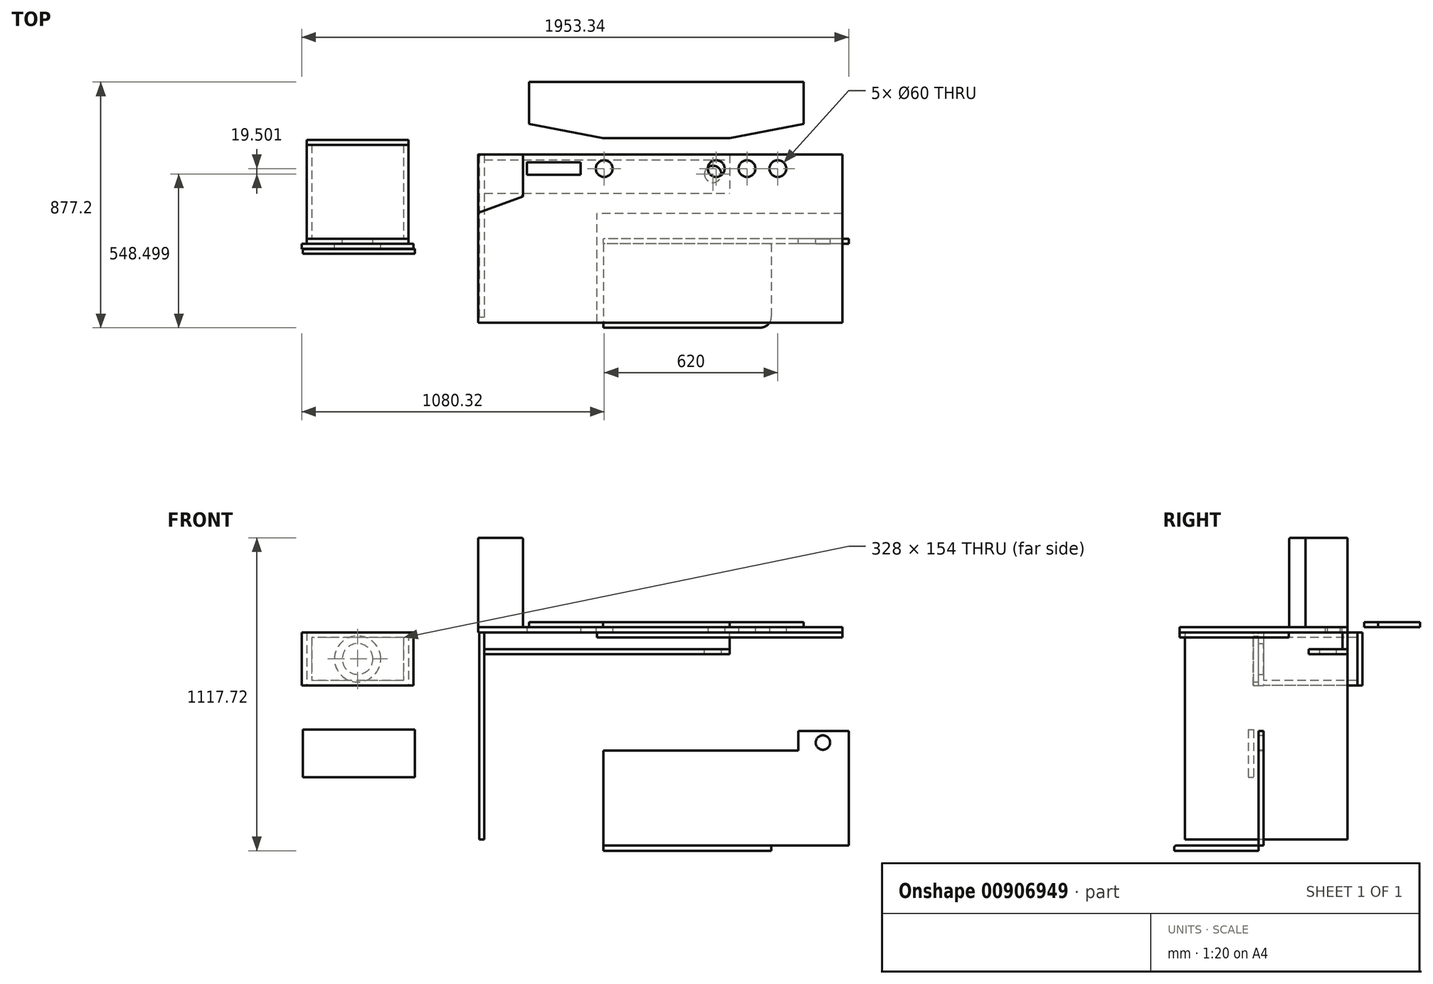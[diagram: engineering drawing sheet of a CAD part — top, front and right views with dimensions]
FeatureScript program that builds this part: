
annotation { "Feature Type Name" : "Feature", "Feature Type Description" : "" }
export const myFeature = defineFeature(function(context is Context, id is Id, definition is map)
    precondition{}
    {
        {
            var Q0;
            Q0=qCreatedBy(makeId("Top.planeOp"),FACE);
            var sketch = newSketch(context, id + "F0", { "sketchPlane" : qUnion([Q0])});
            skLineSegment(sketch, "E0.bottom", {"start": v(650, -300) * mm, "end": v(-650, -300) * mm});
            skLineSegment(sketch, "E0.top", {"start": v(650, 300) * mm, "end": v(-650, 300) * mm});
            skLineSegment(sketch, "E0.left", {"start": v(650, -300) * mm, "end": v(650, 300) * mm});
            skLineSegment(sketch, "E0.right", {"start": v(-650, -300) * mm, "end": v(-650, 300) * mm});
            skPoint(sketch, "E0.middle", {"position": v(0, 0) * mm});
            skLineSegment(sketch, "E1", {"start": v(-650, 250) * mm, "end": v(650, 250) * mm, "construction": true});
            skCircle(sketch, "E2", {"center": v(420, 250) * mm, "radius": 30 * mm});
            skCircle(sketch, "E3.1.0.0", {"center": v(-200, 250) * mm, "radius": 30 * mm});
            skCircle(sketch, "E3.2.0.0", {"center": v(200, 250) * mm, "radius": 30 * mm});
            skCircle(sketch, "E3.3.0.0", {"center": v(310, 250) * mm, "radius": 30 * mm});
            skLineSegment(sketch, "E3.direction1", {"start": v(-200, 250) * mm, "end": v(420, 250) * mm, "construction": true});
            skLineSegment(sketch, "E4.bottom", {"start": v(-284, 227.5) * mm, "end": v(-476, 227.5) * mm});
            skLineSegment(sketch, "E4.top", {"start": v(-284, 272.5) * mm, "end": v(-476, 272.5) * mm});
            skLineSegment(sketch, "E4.left", {"start": v(-284, 227.5) * mm, "end": v(-284, 272.5) * mm});
            skLineSegment(sketch, "E4.right", {"start": v(-476, 227.5) * mm, "end": v(-476, 272.5) * mm});
            skPoint(sketch, "E4.middle", {"position": v(-380, 250) * mm});
            skSolve(sketch);
        }
        {
            var Q0;
            Q0=qSketchRegion(id+"F0",true);
            extrude(context, id + "F1", {"entities" : qUnion([Q0]), "depth" : 18 * mm, "offsetDistance" : 25 * mm});
        }
        {
            var Q0;
            Q0=makeQuery(id+"F1.opExtrude","CAP_FACE",FACE,{"disambiguationData":[OSD([sQuery(id+"F0.wireOp",EDGE,"E0.bottom"),sQuery(id+"F0.wireOp",EDGE,"E0.top"),sQuery(id+"F0.wireOp",EDGE,"E0.left"),sQuery(id+"F0.wireOp",EDGE,"E0.right")])],"isStart":true});
            var sketch = newSketch(context, id + "F2", { "sketchPlane" : qUnion([Q0])});
            skLineSegment(sketch, "E5.bottom", {"start": v(-627.74, -300) * mm, "end": v(248.26, -300) * mm});
            skLineSegment(sketch, "E5.top", {"start": v(-627.74, -282) * mm, "end": v(248.26, -282) * mm});
            skLineSegment(sketch, "E5.left", {"start": v(-627.74, -300) * mm, "end": v(-627.74, -282) * mm});
            skLineSegment(sketch, "E5.right", {"start": v(248.26, -300) * mm, "end": v(248.26, -282) * mm});
            skSolve(sketch);
        }
        {
            var Q0;
            Q0=qSketchRegion(id+"F2",true);
            extrude(context, id + "F3", {"entities" : qUnion([Q0]), "depth" : 60 * mm, "offsetDistance" : 25 * mm});
        }
        {
            var Q0;
            Q0=makeQuery(id+"F3.opExtrude","CAP_FACE",FACE,{"disambiguationData":[OSD([sQuery(id+"F2.wireOp",EDGE,"E5.bottom"),sQuery(id+"F2.wireOp",EDGE,"E5.top"),sQuery(id+"F2.wireOp",EDGE,"E5.left"),sQuery(id+"F2.wireOp",EDGE,"E5.right")])],"isStart":false});
            var sketch = newSketch(context, id + "F4", { "sketchPlane" : qUnion([Q0])});
            skLineSegment(sketch, "E6.bottom", {"start": v(-627.74, -300) * mm, "end": v(248.26, -300) * mm});
            skLineSegment(sketch, "E6.top", {"start": v(-627.74, -162) * mm, "end": v(248.26, -162) * mm});
            skLineSegment(sketch, "E6.left", {"start": v(-627.74, -300) * mm, "end": v(-627.74, -162) * mm});
            skLineSegment(sketch, "E6.right", {"start": v(248.26, -300) * mm, "end": v(248.26, -162) * mm});
            skCircle(sketch, "E7", {"center": v(188.26, -230.5) * mm, "radius": 30 * mm});
            skSolve(sketch);
        }
        {
            var Q0;
            Q0=qSketchRegion(id+"F4",true);
            extrude(context, id + "F5", {"entities" : qUnion([Q0]), "depth" : 18 * mm, "offsetDistance" : 25 * mm});
        }
        {
            var Q0;
            Q0=makeQuery(id+"F3.opExtrude","SWEPT_FACE",FACE,{"disambiguationData":[OSD([sQuery(id+"F2.wireOp",EDGE,"E5.left")])]});
            var sketch = newSketch(context, id + "F6", { "sketchPlane" : qUnion([Q0])});
            skLineSegment(sketch, "E8.bottom", {"start": v(-300, 0) * mm, "end": v(280, 0) * mm});
            skLineSegment(sketch, "E8.top", {"start": v(-300, -740) * mm, "end": v(280, -740) * mm});
            skLineSegment(sketch, "E8.left", {"start": v(-300, 0) * mm, "end": v(-300, -740) * mm});
            skLineSegment(sketch, "E8.right", {"start": v(280, 0) * mm, "end": v(280, -740) * mm});
            skSolve(sketch);
        }
        {
            var Q0;
            Q0=qSketchRegion(id+"F6",true);
            extrude(context, id + "F7", {"entities" : qUnion([Q0]), "depth" : 18 * mm, "offsetDistance" : 25 * mm});
        }
        {
            var Q0;
            Q0=makeQuery(id+"F1.opExtrude","CAP_FACE",FACE,{"disambiguationData":[OSD([sQuery(id+"F0.wireOp",EDGE,"E0.bottom"),sQuery(id+"F0.wireOp",EDGE,"E0.top"),sQuery(id+"F0.wireOp",EDGE,"E0.left"),sQuery(id+"F0.wireOp",EDGE,"E0.right")])],"isStart":false});
            var sketch = newSketch(context, id + "F8", { "sketchPlane" : qUnion([Q0])});
            skLineSegment(sketch, "E9", {"start": v(-650, 300) * mm, "end": v(-650, 91.76) * mm});
            skLineSegment(sketch, "E10", {"start": v(-650, 91.76) * mm, "end": v(-490, 150) * mm});
            skLineSegment(sketch, "E11", {"start": v(-490, 150) * mm, "end": v(-490, 300) * mm});
            skLineSegment(sketch, "E12", {"start": v(-490, 300) * mm, "end": v(-650, 300) * mm});
            skSolve(sketch);
        }
        {
            var Q0;
            Q0=qSketchRegion(id+"F8",true);
            extrude(context, id + "F9", {"entities" : qUnion([Q0]), "depth" : 320 * mm, "offsetDistance" : 25 * mm});
        }
        {
            var Q0;
            Q0=qCreatedBy(makeId("Front.planeOp"),FACE);
            var sketch = newSketch(context, id + "F10", { "sketchPlane" : qUnion([Q0])});
            skLineSegment(sketch, "E13.bottom", {"start": v(-1262.32, 0) * mm, "end": v(-898.32, 0) * mm});
            skLineSegment(sketch, "E13.top", {"start": v(-1262.32, -190) * mm, "end": v(-898.32, -190) * mm});
            skLineSegment(sketch, "E13.left", {"start": v(-1262.32, 0) * mm, "end": v(-1262.32, -190) * mm});
            skLineSegment(sketch, "E13.right", {"start": v(-898.32, 0) * mm, "end": v(-898.32, -190) * mm});
            skCircle(sketch, "E14", {"center": v(-1080.32, -95) * mm, "radius": 55 * mm});
            skPoint(sketch, "E14.centerSnap0", {"position": v(-1080.32, -190) * mm});
            skPoint(sketch, "E14.centerSnap1", {"position": v(-1262.32, -95) * mm});
            skSolve(sketch);
        }
        {
            var Q0;
            Q0=qSketchRegion(id+"F10",true);
            extrude(context, id + "F11", {"entities" : qUnion([Q0]), "depth" : 18 * mm, "offsetDistance" : 25 * mm});
        }
        {
            var Q0;
            Q0=makeQuery(id+"F11.opExtrude","CAP_FACE",FACE,{"disambiguationData":[OSD([sQuery(id+"F10.wireOp",EDGE,"E13.bottom"),sQuery(id+"F10.wireOp",EDGE,"E13.top"),sQuery(id+"F10.wireOp",EDGE,"E13.left"),sQuery(id+"F10.wireOp",EDGE,"E13.right"),sQuery(id+"F10.wireOp",EDGE,"E14")])],"isStart":true});
            var sketch = newSketch(context, id + "F12", { "sketchPlane" : qUnion([Q0])});
            skLineSegment(sketch, "E15.bottom", {"start": v(898.32, 0) * mm, "end": v(1262.32, 0) * mm});
            skLineSegment(sketch, "E15.top", {"start": v(898.32, -190) * mm, "end": v(1262.32, -190) * mm});
            skLineSegment(sketch, "E15.left", {"start": v(898.32, 0) * mm, "end": v(898.32, -190) * mm});
            skLineSegment(sketch, "E15.right", {"start": v(1262.32, 0) * mm, "end": v(1262.32, -190) * mm});
            skLineSegment(sketch, "E16.bottom", {"start": v(916.32, -18) * mm, "end": v(1244.32, -18) * mm});
            skLineSegment(sketch, "E16.top", {"start": v(916.32, -172) * mm, "end": v(1244.32, -172) * mm});
            skLineSegment(sketch, "E16.left", {"start": v(916.32, -18) * mm, "end": v(916.32, -172) * mm});
            skLineSegment(sketch, "E16.right", {"start": v(1244.32, -18) * mm, "end": v(1244.32, -172) * mm});
            skSolve(sketch);
        }
        {
            var Q0;
            Q0=qSketchRegion(id+"F12",true);
            extrude(context, id + "F13", {"entities" : qUnion([Q0]), "depth" : 335 * mm, "offsetDistance" : 25 * mm});
        }
        {
            var Q0;
            Q0=makeQuery(id+"F11.opExtrude","CAP_FACE",FACE,{"disambiguationData":[OSD([sQuery(id+"F10.wireOp",EDGE,"E13.bottom"),sQuery(id+"F10.wireOp",EDGE,"E13.top"),sQuery(id+"F10.wireOp",EDGE,"E13.left"),sQuery(id+"F10.wireOp",EDGE,"E13.right"),sQuery(id+"F10.wireOp",EDGE,"E14")])],"isStart":false});
            var sketch = newSketch(context, id + "F14", { "sketchPlane" : qUnion([Q0])});
            skLineSegment(sketch, "E17.bottom", {"start": v(-880.32, -190) * mm, "end": v(-1280.32, -190) * mm});
            skLineSegment(sketch, "E17.top", {"start": v(-880.32, 0) * mm, "end": v(-1280.32, 0) * mm});
            skLineSegment(sketch, "E17.left", {"start": v(-880.32, -190) * mm, "end": v(-880.32, 0) * mm});
            skLineSegment(sketch, "E17.right", {"start": v(-1280.32, -190) * mm, "end": v(-1280.32, 0) * mm});
            skPoint(sketch, "E17.middle", {"position": v(-1080.32, -95) * mm});
            skCircle(sketch, "E18", {"center": v(-1080.32, -95) * mm, "radius": 82.5 * mm});
            skSolve(sketch);
        }
        {
            var Q0;
            Q0=qSketchRegion(id+"F14",true);
            extrude(context, id + "F15", {"entities" : qUnion([Q0]), "depth" : 18 * mm, "offsetDistance" : 25 * mm});
        }
        {
            var Q0;
            Q0=makeQuery(id+"F13.opExtrude","CAP_FACE",FACE,{"disambiguationData":[OSD([sQuery(id+"F12.wireOp",EDGE,"E15.bottom"),sQuery(id+"F12.wireOp",EDGE,"E15.top"),sQuery(id+"F12.wireOp",EDGE,"E15.left"),sQuery(id+"F12.wireOp",EDGE,"E15.right"),sQuery(id+"F12.wireOp",EDGE,"E16.bottom"),sQuery(id+"F12.wireOp",EDGE,"E16.top"),sQuery(id+"F12.wireOp",EDGE,"E16.left"),sQuery(id+"F12.wireOp",EDGE,"E16.right")])],"isStart":false});
            var sketch = newSketch(context, id + "F16", { "sketchPlane" : qUnion([Q0])});
            skLineSegment(sketch, "E19.bottom", {"start": v(898.32, 0) * mm, "end": v(1262.32, 0) * mm});
            skLineSegment(sketch, "E19.top", {"start": v(898.32, -190) * mm, "end": v(1262.32, -190) * mm});
            skLineSegment(sketch, "E19.left", {"start": v(898.32, 0) * mm, "end": v(898.32, -190) * mm});
            skLineSegment(sketch, "E19.right", {"start": v(1262.32, 0) * mm, "end": v(1262.32, -190) * mm});
            skSolve(sketch);
        }
        {
            var Q0;
            Q0=qSketchRegion(id+"F16",true);
            extrude(context, id + "F17", {"entities" : qUnion([Q0]), "depth" : 18 * mm, "offsetDistance" : 25 * mm});
        }
        {
            var Q0;
            Q0=makeQuery(id+"F1.opExtrude","CAP_FACE",FACE,{"disambiguationData":[OSD([sQuery(id+"F0.wireOp",EDGE,"E0.bottom"),sQuery(id+"F0.wireOp",EDGE,"E0.top"),sQuery(id+"F0.wireOp",EDGE,"E0.left"),sQuery(id+"F0.wireOp",EDGE,"E0.right"),sQuery(id+"F0.wireOp",EDGE,"E2"),sQuery(id+"F0.wireOp",EDGE,"E3.1.0.0"),sQuery(id+"F0.wireOp",EDGE,"E3.2.0.0"),sQuery(id+"F0.wireOp",EDGE,"E3.3.0.0"),sQuery(id+"F0.wireOp",EDGE,"E4.bottom"),sQuery(id+"F0.wireOp",EDGE,"E4.top"),sQuery(id+"F0.wireOp",EDGE,"E4.left"),sQuery(id+"F0.wireOp",EDGE,"E4.right")])],"isStart":true});
            var sketch = newSketch(context, id + "F18", { "sketchPlane" : qUnion([Q0])});
            skLineSegment(sketch, "E20.bottom", {"start": v(650, 300) * mm, "end": v(-226, 300) * mm});
            skLineSegment(sketch, "E20.top", {"start": v(650, -90) * mm, "end": v(-226, -90) * mm});
            skLineSegment(sketch, "E20.left", {"start": v(650, 300) * mm, "end": v(650, -90) * mm});
            skLineSegment(sketch, "E20.right", {"start": v(-226, 300) * mm, "end": v(-226, -90) * mm});
            skSolve(sketch);
        }
        {
            var Q0;
            Q0=qSketchRegion(id+"F18",true);
            extrude(context, id + "F19", {"entities" : qUnion([Q0]), "depth" : 18 * mm, "offsetDistance" : 25 * mm});
        }
        {
            var Q0;
            Q0=qCreatedBy(makeId("Front.planeOp"),FACE);
            var sketch = newSketch(context, id + "F20", { "sketchPlane" : qUnion([Q0])});
            skLineSegment(sketch, "E21.top", {"start": v(673.02, -761.72) * mm, "end": v(-202.98, -761.72) * mm});
            skLineSegment(sketch, "E21.left", {"start": v(673.02, -351.72) * mm, "end": v(673.02, -761.72) * mm});
            skLineSegment(sketch, "E22", {"start": v(673.02, -351.72) * mm, "end": v(493.02, -351.72) * mm});
            skLineSegment(sketch, "E23", {"start": v(493.02, -351.72) * mm, "end": v(493.02, -421.72) * mm});
            skLineSegment(sketch, "E24", {"start": v(493.02, -421.72) * mm, "end": v(-202.98, -421.72) * mm});
            skLineSegment(sketch, "E25", {"start": v(-202.98, -421.72) * mm, "end": v(-202.98, -761.72) * mm});
            skCircle(sketch, "E26", {"center": v(581.1, -393.66) * mm, "radius": 25.73 * mm});
            skSolve(sketch);
        }
        {
            var Q0;
            Q0=qSketchRegion(id+"F20",true);
            extrude(context, id + "F21", {"entities" : qUnion([Q0]), "depth" : 18 * mm, "offsetDistance" : 25 * mm});
        }
        {
            var Q0;
            Q0=makeQuery(id+"F21.opExtrude","SWEPT_FACE",FACE,{"disambiguationData":[OSD([sQuery(id+"F20.wireOp",EDGE,"E21.top")])]});
            var sketch = newSketch(context, id + "F22", { "sketchPlane" : qUnion([Q0])});
            skLineSegment(sketch, "E27.bottom", {"start": v(-202.98, 18) * mm, "end": v(397.02, 18) * mm});
            skLineSegment(sketch, "E27.top", {"start": v(-202.98, 318) * mm, "end": v(357.02, 318) * mm});
            skLineSegment(sketch, "E27.left", {"start": v(-202.98, 18) * mm, "end": v(-202.98, 318) * mm});
            skLineSegment(sketch, "E27.right", {"start": v(397.02, 18) * mm, "end": v(397.02, 278) * mm});
            skPoint(sketch, "E28.visualSharp", {"position": v(397.02, 318) * mm});
            skArc(sketch, "E28.filletArc", {"start": v(397.02, 278) * mm, "mid": v(385.3, 306.28) * mm, "end": v(357.02, 318) * mm});
            skSolve(sketch);
        }
        {
            var Q0;
            Q0=qSketchRegion(id+"F22",true);
            extrude(context, id + "F23", {"entities" : qUnion([Q0]), "depth" : 18 * mm, "offsetDistance" : 25 * mm});
        }
        {
            var Q0;
            Q0=makeQuery(id+"F23.opExtrude","CAP_EDGE",EDGE,{"disambiguationData":[OSD([sQuery(id+"F22.wireOp",EDGE,"E27.top")])],"isStart":true});
            var Q1;
            Q1=makeQuery(id+"F23.opExtrude","CAP_EDGE",EDGE,{"disambiguationData":[OSD([sQuery(id+"F22.wireOp",EDGE,"E28.filletArc")])],"isStart":true});
            var Q2;
            Q2=makeQuery(id+"F23.opExtrude","CAP_EDGE",EDGE,{"disambiguationData":[OSD([sQuery(id+"F22.wireOp",EDGE,"E27.right")])],"isStart":true});
            fillet(context, id + "F24", {"entities" : qUnion([Q0, Q1, Q2]), "radius" : 5 * mm, "tangentPropagation" : true, "allowEdgeOverflow" : false});
        }
        {
            var Q0;
            Q0=makeQuery(id+"F15.opExtrude","CAP_FACE",FACE,{"disambiguationData":[OSD([sQuery(id+"F14.wireOp",EDGE,"E17.bottom"),sQuery(id+"F14.wireOp",EDGE,"E17.top"),sQuery(id+"F14.wireOp",EDGE,"E17.left"),sQuery(id+"F14.wireOp",EDGE,"E17.right"),sQuery(id+"F14.wireOp",EDGE,"E18")])],"isStart":false});
            var sketch = newSketch(context, id + "F25", { "sketchPlane" : qUnion([Q0])});
            skLineSegment(sketch, "E29.bottom", {"start": v(-1276.2, -347.69) * mm, "end": v(-876.2, -347.69) * mm});
            skLineSegment(sketch, "E29.top", {"start": v(-1276.2, -517.69) * mm, "end": v(-876.2, -517.69) * mm});
            skLineSegment(sketch, "E29.left", {"start": v(-1276.2, -347.69) * mm, "end": v(-1276.2, -517.69) * mm});
            skLineSegment(sketch, "E29.right", {"start": v(-876.2, -347.69) * mm, "end": v(-876.2, -517.69) * mm});
            skSolve(sketch);
        }
        {
            var Q0;
            Q0=qSketchRegion(id+"F25",true);
            extrude(context, id + "F26", {"entities" : qUnion([Q0]), "depth" : 18 * mm, "offsetDistance" : 25 * mm});
        }
        {
            var Q0;
            Q0=makeQuery(id+"F15.opExtrude","CAP_FACE",FACE,{"disambiguationData":[OSD([sQuery(id+"F14.wireOp",EDGE,"E17.bottom"),sQuery(id+"F14.wireOp",EDGE,"E17.top"),sQuery(id+"F14.wireOp",EDGE,"E17.left"),sQuery(id+"F14.wireOp",EDGE,"E17.right"),sQuery(id+"F14.wireOp",EDGE,"E18")])],"isStart":false});
            var sketch = newSketch(context, id + "F27", { "sketchPlane" : qUnion([Q0])});
            skLineSegment(sketch, "E30.bottom", {"start": v(-880.32, -190) * mm, "end": v(-1280.32, -190) * mm});
            skLineSegment(sketch, "E30.top", {"start": v(-880.32, 0) * mm, "end": v(-1280.32, 0) * mm});
            skLineSegment(sketch, "E30.left", {"start": v(-880.32, -190) * mm, "end": v(-880.32, 0) * mm});
            skLineSegment(sketch, "E30.right", {"start": v(-1280.32, -190) * mm, "end": v(-1280.32, 0) * mm});
            skSolve(sketch);
        }
        {
            var Q0;
            Q0=qSketchRegion(id+"F27",true);
            extrude(context, id + "F28", {"entities" : qUnion([Q0]), "depth" : 1 * mm, "offsetDistance" : 25 * mm});
        }
        {
            var Q0;
            Q0=makeQuery(id+"F1.opExtrude","CAP_FACE",FACE,{"disambiguationData":[OSD([sQuery(id+"F0.wireOp",EDGE,"E0.bottom"),sQuery(id+"F0.wireOp",EDGE,"E0.top"),sQuery(id+"F0.wireOp",EDGE,"E0.left"),sQuery(id+"F0.wireOp",EDGE,"E0.right"),sQuery(id+"F0.wireOp",EDGE,"E2"),sQuery(id+"F0.wireOp",EDGE,"E3.1.0.0"),sQuery(id+"F0.wireOp",EDGE,"E3.2.0.0"),sQuery(id+"F0.wireOp",EDGE,"E3.3.0.0"),sQuery(id+"F0.wireOp",EDGE,"E4.bottom"),sQuery(id+"F0.wireOp",EDGE,"E4.top"),sQuery(id+"F0.wireOp",EDGE,"E4.left"),sQuery(id+"F0.wireOp",EDGE,"E4.right")])],"isStart":false});
            var sketch = newSketch(context, id + "F29", { "sketchPlane" : qUnion([Q0])});
            skLineSegment(sketch, "E31.top", {"start": v(-468.02, 559.2) * mm, "end": v(511.98, 559.2) * mm});
            skLineSegment(sketch, "E32", {"start": v(-468.02, 559.2) * mm, "end": v(-468.02, 409.2) * mm});
            skLineSegment(sketch, "E33", {"start": v(-468.02, 409.2) * mm, "end": v(-204.45, 359.2) * mm});
            skLineSegment(sketch, "E34", {"start": v(-204.45, 359.2) * mm, "end": v(248.41, 359.2) * mm});
            skLineSegment(sketch, "E35", {"start": v(248.41, 359.2) * mm, "end": v(511.98, 409.2) * mm});
            skLineSegment(sketch, "E36", {"start": v(511.98, 559.2) * mm, "end": v(511.98, 409.2) * mm});
            skSolve(sketch);
        }
        {
            var Q0;
            Q0 = qSketchRegion(id + "F29", true);
            extrude(context, id + "F30", {"entities" : qUnion([Q0]), "depth" : 18 * mm, "offsetDistance" : 25 * mm});
        }
        {
            var Q0;
            Q0=makeQuery(id+"F9.opExtrude","CAP_EDGE",EDGE,{"disambiguationData":[OSD([sQuery(id+"F8.wireOp",EDGE,"E9")])],"isStart":false});
            var Q1;
            Q1=makeQuery(id+"F9.opExtrude","CAP_EDGE",EDGE,{"disambiguationData":[OSD([sQuery(id+"F8.wireOp",EDGE,"E10")])],"isStart":false});
            var Q2;
            Q2=makeQuery(id+"F9.opExtrude","CAP_EDGE",EDGE,{"disambiguationData":[OSD([sQuery(id+"F8.wireOp",EDGE,"E11")])],"isStart":false});
            var Q3;
            Q3=makeQuery(id+"F9.opExtrude","CAP_EDGE",EDGE,{"disambiguationData":[OSD([sQuery(id+"F8.wireOp",EDGE,"E12")])],"isStart":false});
            var Q4;
            Q4=makeQuery(id+"F9.opExtrude","CAP_EDGE",EDGE,{"disambiguationData":[OSD([sQuery(id+"F8.wireOp",EDGE,"E10")])],"isStart":true});
            var Q5;
            Q5=makeQuery(id+"F9.opExtrude","CAP_EDGE",EDGE,{"disambiguationData":[OSD([sQuery(id+"F8.wireOp",EDGE,"E11")])],"isStart":true});
            var Q6;
            Q6=makeQuery(id+"F9.opExtrude","CAP_EDGE",EDGE,{"disambiguationData":[OSD([sQuery(id+"F8.wireOp",EDGE,"E12")])],"isStart":true});
            var Q7;
            Q7=makeQuery(id+"F9.opExtrude","CAP_EDGE",EDGE,{"disambiguationData":[OSD([sQuery(id+"F8.wireOp",EDGE,"E9")])],"isStart":true});
            fillet(context, id + "F31", {"entities" : qUnion([Q0, Q1, Q2, Q3, Q4, Q5, Q6, Q7]), "radius" : 5 * mm, "tangentPropagation" : true, "allowEdgeOverflow" : false});
        }
    });
